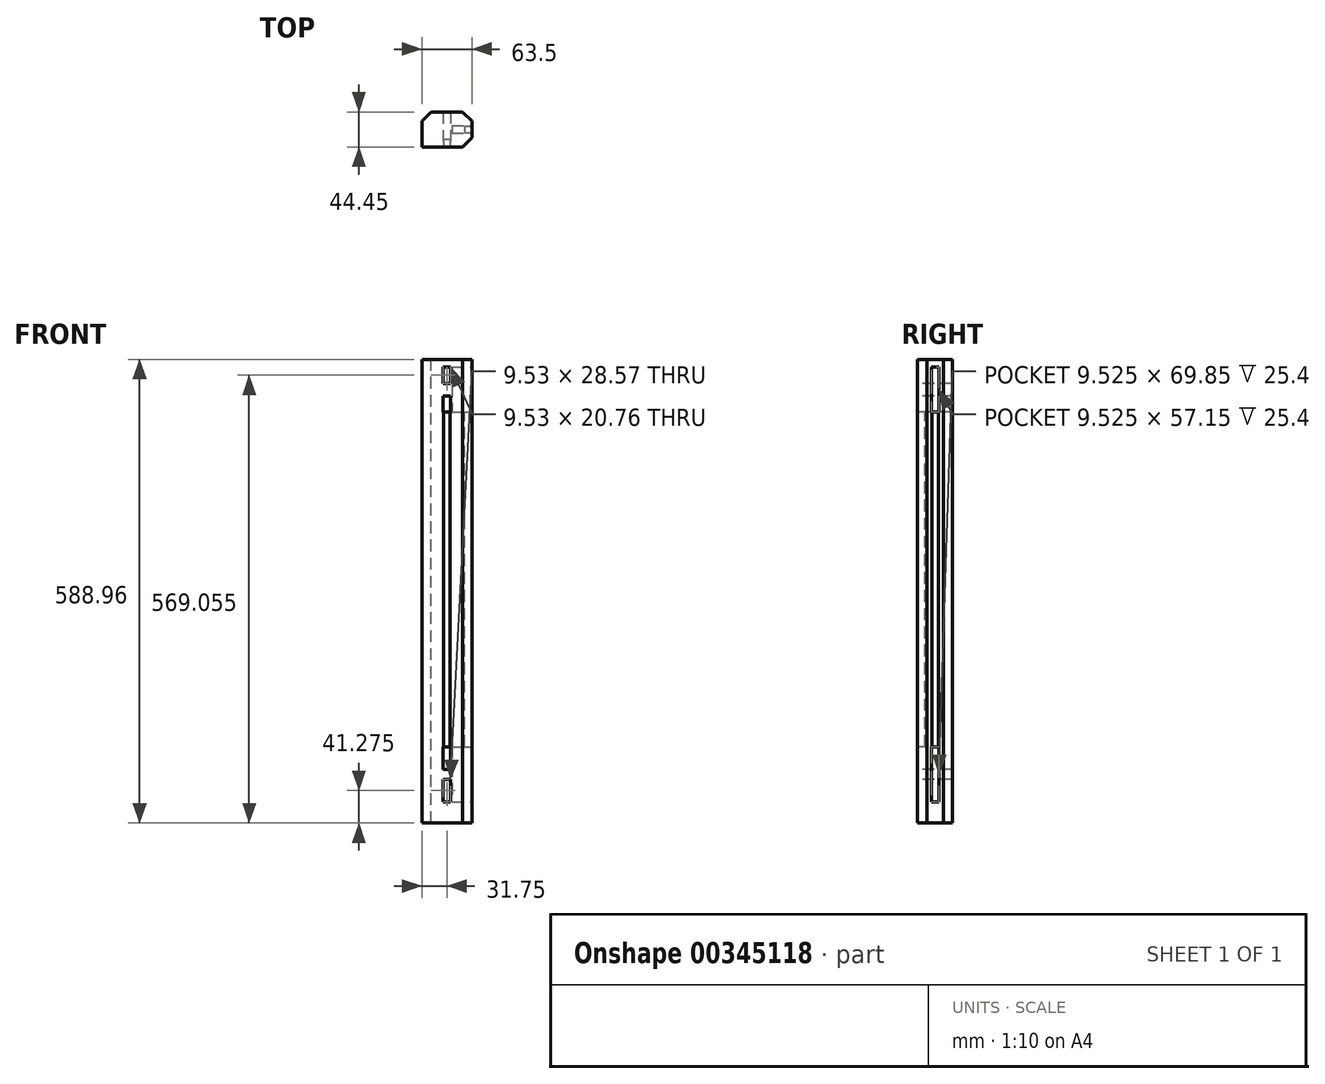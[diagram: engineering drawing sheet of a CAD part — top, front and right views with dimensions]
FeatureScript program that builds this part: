
annotation { "Feature Type Name" : "Feature", "Feature Type Description" : "" }
export const myFeature = defineFeature(function(context is Context, id is Id, definition is map)
    precondition{}
    {
        {
            var Q0;
            Q0=qCreatedBy(makeId("Top.planeOp"),FACE);
            var sketch = newSketch(context, id + "F0", { "sketchPlane" : qUnion([Q0])});
            skLineSegment(sketch, "E0", {"start": v(0, 0) * mm, "end": v(63.5, 0) * mm});
            skLineSegment(sketch, "E1", {"start": v(63.5, 0) * mm, "end": v(63.5, 44.45) * mm});
            skLineSegment(sketch, "E2", {"start": v(63.5, 44.45) * mm, "end": v(0, 44.45) * mm});
            skLineSegment(sketch, "E3", {"start": v(0, 44.45) * mm, "end": v(0, 0) * mm});
            skSolve(sketch);
        }
        {
            var Q0;
            Q0 = qSketchRegion(id + "F0", true);
            extrude(context, id + "F1", {"entities" : qUnion([Q0]), "depth" : 588.96 * mm});
        }
        {
            var Q0;
            Q0=makeQuery(id+"F1.opExtrude","SWEPT_FACE",FACE,{"disambiguationData":[OSD([sQuery(id+"F0.wireOp",EDGE,"E1")])]});
            var sketch = newSketch(context, id + "F2", { "sketchPlane" : qUnion([Q0])});
            skLineSegment(sketch, "E4", {"start": v(17.46, 579.44) * mm, "end": v(17.46, 522.29) * mm});
            skLineSegment(sketch, "E5", {"start": v(17.46, 522.29) * mm, "end": v(26.99, 522.29) * mm});
            skLineSegment(sketch, "E6", {"start": v(26.99, 522.29) * mm, "end": v(26.99, 579.44) * mm});
            skLineSegment(sketch, "E7", {"start": v(26.99, 579.44) * mm, "end": v(17.46, 579.44) * mm});
            skLineSegment(sketch, "E8", {"start": v(17.46, 96.84) * mm, "end": v(17.46, 26.99) * mm});
            skLineSegment(sketch, "E9", {"start": v(17.46, 26.99) * mm, "end": v(26.99, 26.99) * mm});
            skLineSegment(sketch, "E10", {"start": v(26.99, 26.99) * mm, "end": v(26.99, 96.84) * mm});
            skLineSegment(sketch, "E11", {"start": v(26.99, 96.84) * mm, "end": v(17.46, 96.84) * mm});
            skPoint(sketch, "E12", {"position": v(18.26, 96.84) * mm});
            skPoint(sketch, "E13", {"position": v(26.2, 96.84) * mm});
            skPoint(sketch, "E14", {"position": v(18.26, 522.29) * mm});
            skPoint(sketch, "E15", {"position": v(26.2, 522.29) * mm});
            skLineSegment(sketch, "E16", {"start": v(18.26, 522.29) * mm, "end": v(18.26, 96.84) * mm});
            skLineSegment(sketch, "E17", {"start": v(26.2, 96.84) * mm, "end": v(26.2, 522.29) * mm});
            skSolve(sketch);
        }
        {
            var Q0;
            {var subQ4=sQuery(id+"F2.wireOp",EDGE,"E4");Q0=makeQuery(id+"F2.imprint","IMPRINT",FACE,{"disambiguationData":[TD([[makeQuery(id+"F2.imprint","IMPRINT",EDGE,{"derivedFrom":subQ4}),1.0]])]});}
            var Q1;
            {var subQ3=sQuery(id+"F2.wireOp",EDGE,"E8");Q1=makeQuery(id+"F2.imprint","IMPRINT",FACE,{"disambiguationData":[TD([[makeQuery(id+"F2.imprint","IMPRINT",EDGE,{"derivedFrom":subQ3}),1.0]])]});}
            extrude(context, id + "F3", {"entities" : qUnion([Q0, Q1]), "operationType" : NewBodyOperationType.REMOVE, "oppositeDirection" : true, "depth" : 25.4 * mm});
        }
        {
            var Q0;
            {var subQ0=sQuery(id+"F2.wireOp",EDGE,"E16");Q0=makeQuery(id+"F2.imprint","IMPRINT",FACE,{"disambiguationData":[TD([[makeQuery(id+"F2.imprint","IMPRINT",EDGE,{"derivedFrom":subQ0}),1.0]])]});}
            extrude(context, id + "F4", {"entities" : qUnion([Q0]), "operationType" : NewBodyOperationType.REMOVE, "oppositeDirection" : true, "depth" : 9.52 * mm});
        }
        {
            var Q0;
            Q0=makeQuery(id+"F1.opExtrude","SWEPT_FACE",FACE,{"disambiguationData":[OSD([sQuery(id+"F0.wireOp",EDGE,"E0")])]});
            var sketch = newSketch(context, id + "F5", { "sketchPlane" : qUnion([Q0])});
            skLineSegment(sketch, "E18", {"start": v(26.99, 579.44) * mm, "end": v(26.99, 558.67) * mm});
            skLineSegment(sketch, "E19", {"start": v(26.99, 558.67) * mm, "end": v(36.51, 558.67) * mm});
            skLineSegment(sketch, "E20", {"start": v(36.51, 558.67) * mm, "end": v(36.51, 579.44) * mm});
            skLineSegment(sketch, "E21", {"start": v(36.51, 579.44) * mm, "end": v(26.99, 579.44) * mm});
            skPoint(sketch, "E22.startSnap0", {"position": v(26.99, 569.06) * mm});
            skLineSegment(sketch, "E23", {"start": v(26.99, 55.56) * mm, "end": v(36.51, 55.56) * mm});
            skLineSegment(sketch, "E24", {"start": v(28.57, 522.03) * mm, "end": v(26.99, 522.03) * mm});
            skLineSegment(sketch, "E25", {"start": v(26.99, 522.03) * mm, "end": v(26.99, 522.03) * mm});
            skLineSegment(sketch, "E26", {"start": v(26.99, 522.03) * mm, "end": v(26.99, 542.8) * mm});
            skLineSegment(sketch, "E27", {"start": v(26.99, 542.8) * mm, "end": v(36.51, 542.8) * mm});
            skLineSegment(sketch, "E28", {"start": v(36.51, 542.8) * mm, "end": v(36.51, 522.03) * mm});
            skLineSegment(sketch, "E29", {"start": v(36.51, 522.03) * mm, "end": v(28.57, 522.03) * mm});
            skLineSegment(sketch, "E30", {"start": v(26.99, 55.56) * mm, "end": v(26.99, 55.56) * mm});
            skLineSegment(sketch, "E31", {"start": v(26.99, 55.56) * mm, "end": v(26.99, 26.99) * mm});
            skLineSegment(sketch, "E32", {"start": v(36.51, 55.56) * mm, "end": v(36.51, 26.99) * mm});
            skLineSegment(sketch, "E33", {"start": v(36.51, 26.99) * mm, "end": v(26.99, 26.99) * mm});
            skLineSegment(sketch, "E34", {"start": v(36.51, 68.26) * mm, "end": v(36.51, 96.84) * mm});
            skLineSegment(sketch, "E35", {"start": v(36.51, 96.84) * mm, "end": v(26.99, 96.84) * mm});
            skLineSegment(sketch, "E36", {"start": v(26.99, 96.84) * mm, "end": v(26.99, 68.26) * mm});
            skLineSegment(sketch, "E37", {"start": v(26.99, 68.26) * mm, "end": v(36.51, 68.26) * mm});
            skPoint(sketch, "E38", {"position": v(35.72, 96.84) * mm});
            skPoint(sketch, "E39", {"position": v(27.78, 96.84) * mm});
            skLineSegment(sketch, "E40", {"start": v(35.72, 96.84) * mm, "end": v(35.72, 522.03) * mm});
            skLineSegment(sketch, "E41", {"start": v(27.78, 96.84) * mm, "end": v(27.78, 522.03) * mm});
            skSolve(sketch);
        }
        {
            var Q0;
            {var subQ0=sQuery(id+"F5.wireOp",EDGE,"E40");Q0=makeQuery(id+"F5.imprint","IMPRINT",FACE,{"disambiguationData":[TD([[makeQuery(id+"F5.imprint","IMPRINT",EDGE,{"derivedFrom":subQ0}),1.0]])]});}
            extrude(context, id + "F6", {"entities" : qUnion([Q0]), "operationType" : NewBodyOperationType.REMOVE, "oppositeDirection" : true, "depth" : 9.52 * mm});
        }
        {
            var Q0;
            Q0=makeQuery(id+"F5.imprint","IMPRINT",FACE,{"disambiguationData":[TD([[makeQuery(id+"F5.imprint","IMPRINT",EDGE,{"derivedFrom":sQuery(id+"F5.wireOp",EDGE,"E18")}),1.0]])]});
            var Q1;
            {var subQ0=sQuery(id+"F5.wireOp",EDGE,"E26");Q1=makeQuery(id+"F5.imprint","IMPRINT",FACE,{"disambiguationData":[TD([[makeQuery(id+"F5.imprint","IMPRINT",EDGE,{"derivedFrom":subQ0}),-1.0]])]});}
            var Q2;
            {var subQ4=sQuery(id+"F5.wireOp",EDGE,"E34");Q2=makeQuery(id+"F5.imprint","IMPRINT",FACE,{"disambiguationData":[TD([[makeQuery(id+"F5.imprint","IMPRINT",EDGE,{"derivedFrom":subQ4}),1.0]])]});}
            var Q3;
            Q3=makeQuery(id+"F5.imprint","IMPRINT",FACE,{"disambiguationData":[TD([[makeQuery(id+"F5.imprint","IMPRINT",EDGE,{"derivedFrom":sQuery(id+"F5.wireOp",EDGE,"E23")}),-1.0]])]});
            extrude(context, id + "F7", {"entities" : qUnion([Q0, Q1, Q2, Q3]), "operationType" : NewBodyOperationType.REMOVE, "endBound" : BoundingType.THROUGH_ALL, "oppositeDirection" : true, "depth" : 25.4 * mm});
        }
        {
            var Q0;
            Q0=makeQuery(id+"F1.opExtrude","SWEPT_EDGE",EDGE,{"disambiguationData":[OSD([sQuery(id+"F0.wireOp",EDGE,"E1"),sQuery(id+"F0.wireOp",EDGE,"E2")])]});
            var Q1;
            Q1=makeQuery(id+"F1.opExtrude","SWEPT_EDGE",EDGE,{"disambiguationData":[OSD([sQuery(id+"F0.wireOp",EDGE,"E2"),sQuery(id+"F0.wireOp",EDGE,"E3")])]});
            var Q2;
            Q2=makeQuery(id+"F1.opExtrude","SWEPT_EDGE",EDGE,{"disambiguationData":[OSD([sQuery(id+"F0.wireOp",EDGE,"E0"),sQuery(id+"F0.wireOp",EDGE,"E1")])]});
            chamfer(context, id + "F8", {"entities" : qUnion([Q0, Q1, Q2]), "width" : 11.9 * mm, "tangentPropagation" : true});
        }
    });
